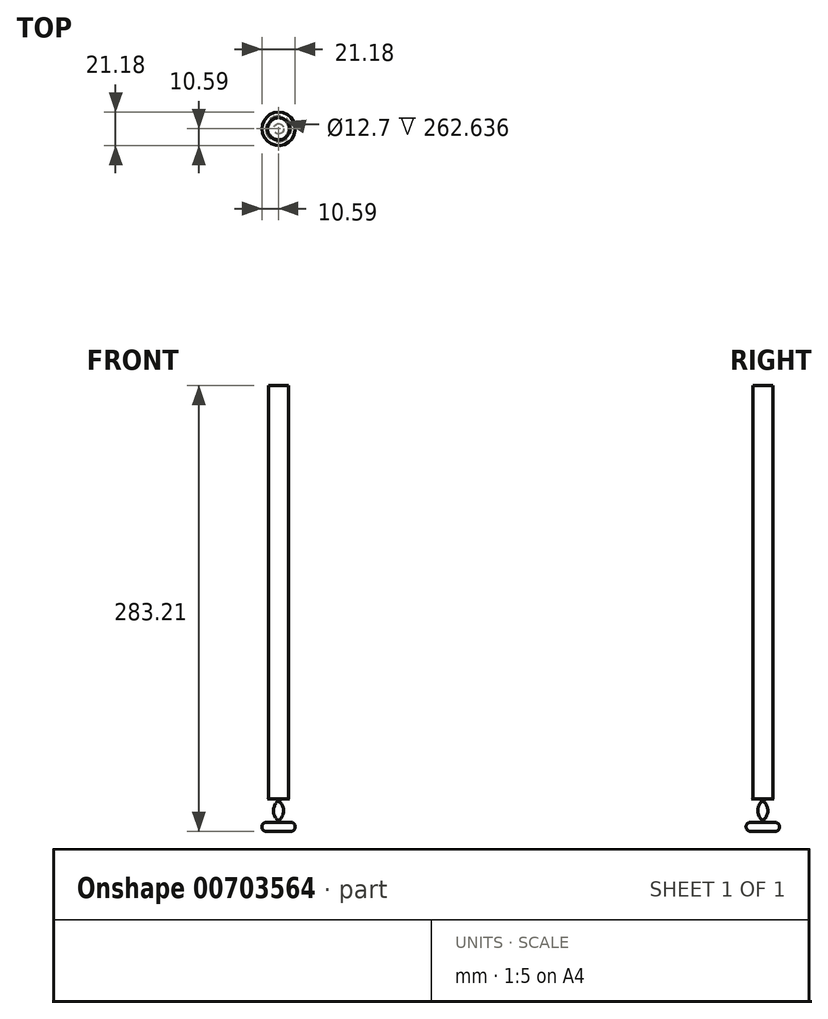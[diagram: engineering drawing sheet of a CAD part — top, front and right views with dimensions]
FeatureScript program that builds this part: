
annotation { "Feature Type Name" : "Feature", "Feature Type Description" : "" }
export const myFeature = defineFeature(function(context is Context, id is Id, definition is map)
    precondition{}
    {
        {
            var Q0;
            Q0=qCreatedBy(makeId("Top.planeOp"),FACE);
            var sketch = newSketch(context, id + "F0", { "sketchPlane" : qUnion([Q0])});
            skCircle(sketch, "E0", {"center": v(0, 0) * mm, "radius": 6.35 * mm});
            skCircle(sketch, "E1", {"center": v(0, 0) * mm, "radius": 12.7 * mm});
            skSolve(sketch);
        }
        {
            var Q0;
            Q0=makeQuery(id+"F0.imprint","IMPRINT",FACE,{"disambiguationData":[TD([[makeQuery(id+"F0.imprint","IMPRINT",EDGE,{"derivedFrom":sQuery(id+"F0.wireOp",EDGE,"E0")}),1.0]])]});
            extrude(context, id + "F1", {"entities" : qUnion([Q0]), "depth" : 262.64 * mm, "offsetDistance" : 25.4 * mm});
        }
        {
            var Q0;
            Q0=makeQuery(id+"F0.imprint","IMPRINT",FACE,{"disambiguationData":[TD([[makeQuery(id+"F0.imprint","IMPRINT",EDGE,{"derivedFrom":sQuery(id+"F0.wireOp",EDGE,"E0")}),-1.0]])]});
            var Q1;
            Q1=makeQuery(id+"F0.imprint","IMPRINT",FACE,{"disambiguationData":[TD([[makeQuery(id+"F0.imprint","IMPRINT",EDGE,{"derivedFrom":sQuery(id+"F0.wireOp",EDGE,"E0")}),1.0]])]});
            extrude(context, id + "F2", {"entities" : qUnion([Q0, Q1]), "operationType" : NewBodyOperationType.ADD, "oppositeDirection" : true, "depth" : 20.57 * mm, "offsetDistance" : 25.4 * mm});
        }
        {
            var Q0;
            Q0=qCreatedBy(makeId("Front.planeOp"),FACE);
            var sketch = newSketch(context, id + "F3", { "sketchPlane" : qUnion([Q0])});
            skLineSegment(sketch, "E2", {"start": v(0, 3.38) * mm, "end": v(0, -25.93) * mm});
            skLineSegment(sketch, "E3", {"start": v(7.07, -25.93) * mm, "end": v(17.55, -25.93) * mm});
            skLineSegment(sketch, "E4", {"start": v(17.55, -25.93) * mm, "end": v(17.55, 2.82) * mm});
            skLineSegment(sketch, "E5", {"start": v(17.55, 2.82) * mm, "end": v(7.07, 2.82) * mm});
            skLineSegment(sketch, "E6", {"start": v(7.07, 2.82) * mm, "end": v(7.07, -25.93) * mm});
            skPoint(sketch, "E7", {"position": v(7.07, -14.79) * mm});
            skPoint(sketch, "E8", {"position": v(7.07, 0) * mm});
            skPoint(sketch, "E9", {"position": v(7.07, -20.58) * mm});
            skArc(sketch, "E10", {"start": v(7.07, -14.79) * mm, "mid": v(12.38, -7.4) * mm, "end": v(7.07, 0) * mm});
            skArc(sketch, "E11", {"start": v(7.07, -20.58) * mm, "mid": v(10.6, -17.68) * mm, "end": v(7.07, -14.79) * mm});
            skSolve(sketch);
        }
        {
            var Q0;
            {var subQ3=sQuery(id+"F3.wireOp",EDGE,"E3");Q0=makeQuery(id+"F3.imprint","IMPRINT",FACE,{"disambiguationData":[TD([[makeQuery(id+"F3.imprint","IMPRINT",EDGE,{"derivedFrom":subQ3}),1.0]])]});}
            var Q1;
            Q1=sQuery(id+"F3.wireOp",EDGE,"E2");
            revolve(context, id + "F4", {"operationType" : NewBodyOperationType.REMOVE, "surfaceOperationType" : NewSurfaceOperationType.NEW, "entities" : qUnion([Q0]), "axis" : qUnion([Q1]), "revolveType" : RevolveType.FULL, "oppositeDirection" : true});
        }
    });
